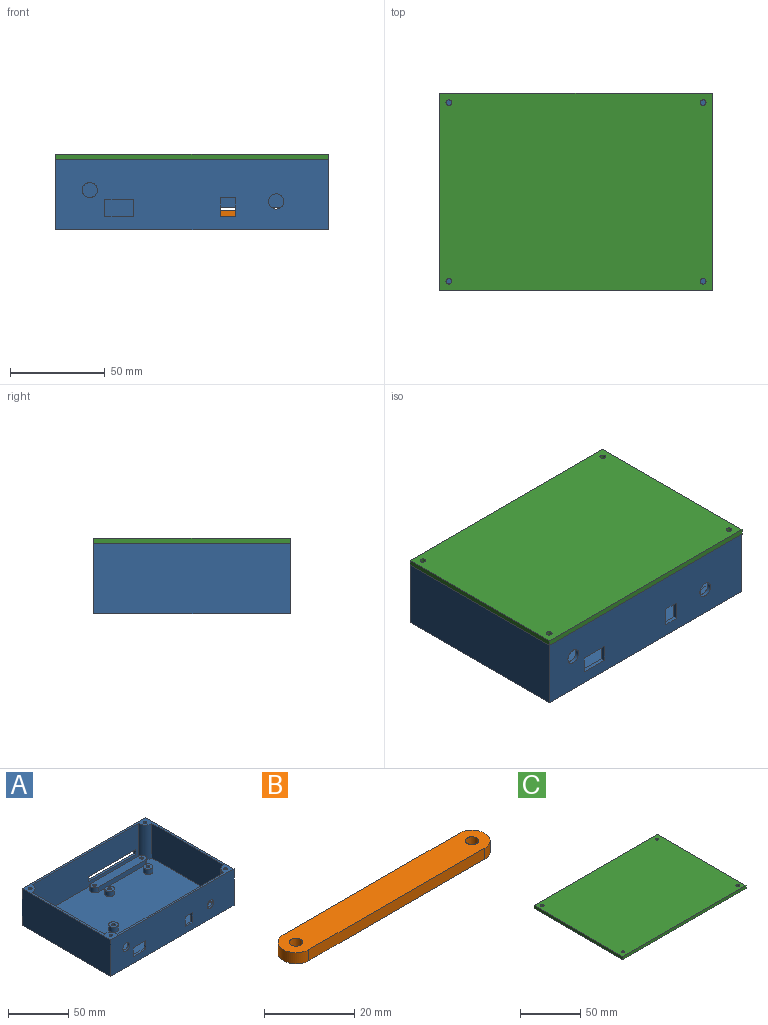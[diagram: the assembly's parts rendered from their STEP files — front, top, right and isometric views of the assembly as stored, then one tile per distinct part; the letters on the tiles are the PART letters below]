
ASSEMBLY  parts=3 mates=2
PART A: 65 faces, bbox 144x104x37 mm
  f0: plane 144x104mm, normal (0,0,1), area 1148.8mm2, adj f1,f2,f3,f4,f6,f7,f9,f10
  f1: plane 144x37mm, normal (0,1,0), area 5053mm2, adj f0,f6,f7,f8,f53,f54,f55,f56
  f2: plane 124x35mm, normal (0,-1,0), area 4065mm2, adj f0,f5,f13,f14,f53,f54,f55,f56
  f3: plane 144x37mm, normal (0,-1,0), area 5012.5mm2, adj f0,f6,f7,f8,f21,f44,f45,f46
  f4: plane 124x35mm, normal (0,1,0), area 3864.5mm2, adj f0,f5,f10,f11,f15,f17,f19,f21
  f5: plane 140x100mm, normal (0,0,1), area 12956.8mm2, adj f2,f4,f9,f10,f11,f12,f13,f14
  f6: plane 104x37mm, normal (-1,0,0), area 3848mm2, adj f0,f1,f3,f8
  f7: plane 104x37mm, normal (1,0,0), area 3848mm2, adj f0,f1,f3,f8
  f8: plane 144x104mm, normal (0,0,-1), area 14976mm2, adj f1,f3,f6,f7
  f9: plane 84x35mm, normal (-1,0,0), area 2940mm2, adj f0,f5,f10,f14
  f10: cylinder r=8mm len=35mm, axis (0,0,-1), area 439.8mm2, adj f0,f4,f5,f9,f15
  f11: cylinder r=8mm len=35mm, axis (0,0,-1), area 439.8mm2, adj f0,f4,f5,f12
  f12: plane 84x35mm, normal (1,0,0), area 2940mm2, adj f0,f5,f11,f13
  f13: cylinder r=8mm len=35mm, axis (0,0,-1), area 439.8mm2, adj f0,f2,f5,f12
  f14: cylinder r=8mm len=35mm, axis (0,0,-1), area 439.8mm2, adj f0,f2,f5,f9
  f15: cylinder r=8mm len=16mm, axis (0,0,-1), area 125.7mm2, adj f4,f5,f10,f17
  f16: cylinder r=1.5mm len=5mm, axis (0,0,-1), area 47.1mm2, adj f17,f18
  f17: plane 16x8mm, normal (0,0,1), area 93.5mm2, adj f4,f15,f16
  f18: plane 3x3mm, normal (0,0,1), area 7.1mm2, adj f16
  f19: cylinder r=8mm len=16mm, axis (0,0,-1), area 125.7mm2, adj f4,f5,f21
  f20: cylinder r=1.5mm len=5mm, axis (0,0,-1), area 47.1mm2, adj f21,f22
  f21: plane 22x10mm, normal (0,0,1), area 109.5mm2, adj f3,f4,f19,f20,f44,f46
  f22: plane 3x3mm, normal (0,0,1), area 7.1mm2, adj f20
  f23: cylinder r=1.5mm len=5mm, axis (0,0,-1), area 47.1mm2, adj f25,f26
  f24: cylinder r=4mm len=8mm, axis (0,0,-1), area 125.7mm2, adj f5,f25
  f25: plane 8x8mm, normal (0,0,1), area 43.2mm2, adj f23,f24
  f26: plane 3x3mm, normal (0,0,1), area 7.1mm2, adj f23
  f27: cylinder r=1.5mm len=5mm, axis (0,0,-1), area 47.1mm2, adj f29,f30
  f28: cylinder r=4mm len=8mm, axis (0,0,-1), area 125.7mm2, adj f5,f29
  f29: plane 8x8mm, normal (0,0,1), area 43.2mm2, adj f27,f28
  f30: plane 3x3mm, normal (0,0,1), area 7.1mm2, adj f27
  f31: plane 55x5mm, normal (0,1,0), area 275mm2, adj f5,f32,f35,f37
  f32: cylinder r=4mm len=8mm, axis (0,0,-1), area 62.8mm2, adj f5,f31,f33,f37
  f33: plane 55x5mm, normal (0,-1,0), area 275mm2, adj f5,f32,f35,f37
  f34: cylinder r=1.5mm len=5mm, axis (0,0,-1), area 47.1mm2, adj f37,f39
  f35: cylinder r=4mm len=8mm, axis (0,0,-1), area 62.8mm2, adj f5,f31,f33,f37
  f36: cylinder r=1.5mm len=5mm, axis (0,0,-1), area 47.1mm2, adj f37,f38
  f37: plane 63x8mm, normal (0,0,1), area 476.1mm2, adj f31,f32,f33,f34,f35,f36
  f38: plane 3x3mm, normal (0,0,1), area 7.1mm2, adj f36
  f39: plane 3x3mm, normal (0,0,1), area 7.1mm2, adj f34
  f40: cylinder r=1.5mm len=5mm, axis (0,0,-1), area 47.1mm2, adj f42,f43
  f41: cylinder r=4mm len=8mm, axis (0,0,-1), area 125.7mm2, adj f5,f42
  f42: plane 8x8mm, normal (0,0,1), area 43.2mm2, adj f40,f41
  f43: plane 3x3mm, normal (0,0,1), area 7.1mm2, adj f40
  f44: plane 10x2mm, normal (1,0,0), area 20mm2, adj f3,f4,f21,f45
  f45: plane 8x2mm, normal (0,0,-1), area 16mm2, adj f3,f4,f44,f46
  f46: plane 10x2mm, normal (-1,0,0), area 20mm2, adj f3,f4,f21,f45
  f47: cylinder r=4mm len=8mm, axis (0,1,0), area 50.3mm2, adj f3,f4
  f48: plane 9x2mm, normal (-1,0,0), area 18mm2, adj f3,f4,f49,f51
  f49: plane 15x2mm, normal (0,0,1), area 30mm2, adj f3,f4,f48,f50
  f50: plane 9x2mm, normal (1,0,0), area 18mm2, adj f3,f4,f49,f51
  f51: plane 15x2mm, normal (0,0,-1), area 30mm2, adj f3,f4,f48,f50
  f52: cylinder r=4mm len=8mm, axis (0,1,0), area 50.3mm2, adj f3,f4
  f53: plane 55x2mm, normal (0,0,-1), area 110mm2, adj f1,f2,f54,f56
  f54: plane 5x2mm, normal (1,0,0), area 10mm2, adj f1,f2,f53,f55
  f55: plane 55x2mm, normal (0,0,1), area 110mm2, adj f1,f2,f54,f56
  f56: plane 5x2mm, normal (-1,0,0), area 10mm2, adj f1,f2,f53,f55
  f57: cylinder r=1.5mm len=20mm, axis (0,0,1), area 188.5mm2, adj f0,f58
  f58: plane 3x3mm, normal (0,0,1), area 7.1mm2, adj f57
  f59: cylinder r=1.5mm len=20mm, axis (0,0,1), area 188.5mm2, adj f0,f60
  f60: plane 3x3mm, normal (0,0,1), area 7.1mm2, adj f59
  f61: cylinder r=1.5mm len=20mm, axis (0,0,1), area 188.5mm2, adj f0,f62
  f62: plane 3x3mm, normal (0,0,1), area 7.1mm2, adj f61
  f63: cylinder r=1.5mm len=20mm, axis (0,0,1), area 188.5mm2, adj f0,f64
  f64: plane 3x3mm, normal (0,0,1), area 7.1mm2, adj f63
PART B: 8 faces, bbox 63x8x3 mm
  f0: plane 55x3mm, normal (0,1,0), area 165mm2, adj f1,f4,f6,f7
  f1: cylinder r=4mm len=8mm, axis (0,0,-1), area 37.7mm2, adj f0,f2,f6,f7
  f2: plane 55x3mm, normal (0,-1,0), area 165mm2, adj f1,f4,f6,f7
  f3: cylinder r=1.5mm len=3mm, axis (0,0,-1), area 28.3mm2, adj f6,f7
  f4: cylinder r=4mm len=8mm, axis (0,0,-1), area 37.7mm2, adj f0,f2,f6,f7
  f5: cylinder r=1.5mm len=3mm, axis (0,0,-1), area 28.3mm2, adj f6,f7
  f6: plane 63x8mm, normal (0,0,1), area 476.1mm2, adj f0,f1,f2,f3,f4,f5
  f7: plane 63x8mm, normal (0,0,-1), area 476.1mm2, adj f0,f1,f2,f3,f4,f5
PART C: 10 faces, bbox 144x104x3 mm
  f0: plane 144x3mm, normal (0,1,0), area 432mm2, adj f1,f6,f8,f9
  f1: plane 104x3mm, normal (-1,0,0), area 312mm2, adj f0,f2,f8,f9
  f2: plane 144x3mm, normal (0,-1,0), area 432mm2, adj f1,f6,f8,f9
  f3: cylinder r=1.5mm len=3mm, axis (0,0,-1), area 28.3mm2, adj f8,f9
  f4: cylinder r=1.5mm len=3mm, axis (0,0,-1), area 28.3mm2, adj f8,f9
  f5: cylinder r=1.5mm len=3mm, axis (0,0,-1), area 28.3mm2, adj f8,f9
  f6: plane 104x3mm, normal (1,0,0), area 312mm2, adj f0,f2,f8,f9
  f7: cylinder r=1.5mm len=3mm, axis (0,0,-1), area 28.3mm2, adj f8,f9
  f8: plane 144x104mm, normal (0,0,1), area 14947.7mm2, adj f0,f1,f2,f3,f4,f5,f6,f7
  f9: plane 144x104mm, normal (0,0,-1), area 14947.7mm2, adj f0,f1,f2,f3,f4,f5,f6,f7
PLACE A t=(5.78,-43.48,11.98)mm
PLACE B t=(70.1,45.52,18.98)mm
PLACE C t=(3.78,-45.48,48.98)mm
MATE parallel C.f9 <-> A.f0  axis (0,0,-1) through (75.78,6.52,48.98)mm
MATE parallel A.f37 <-> B.f7  axis (0,0,1) through (107.28,49.52,18.98)mm
